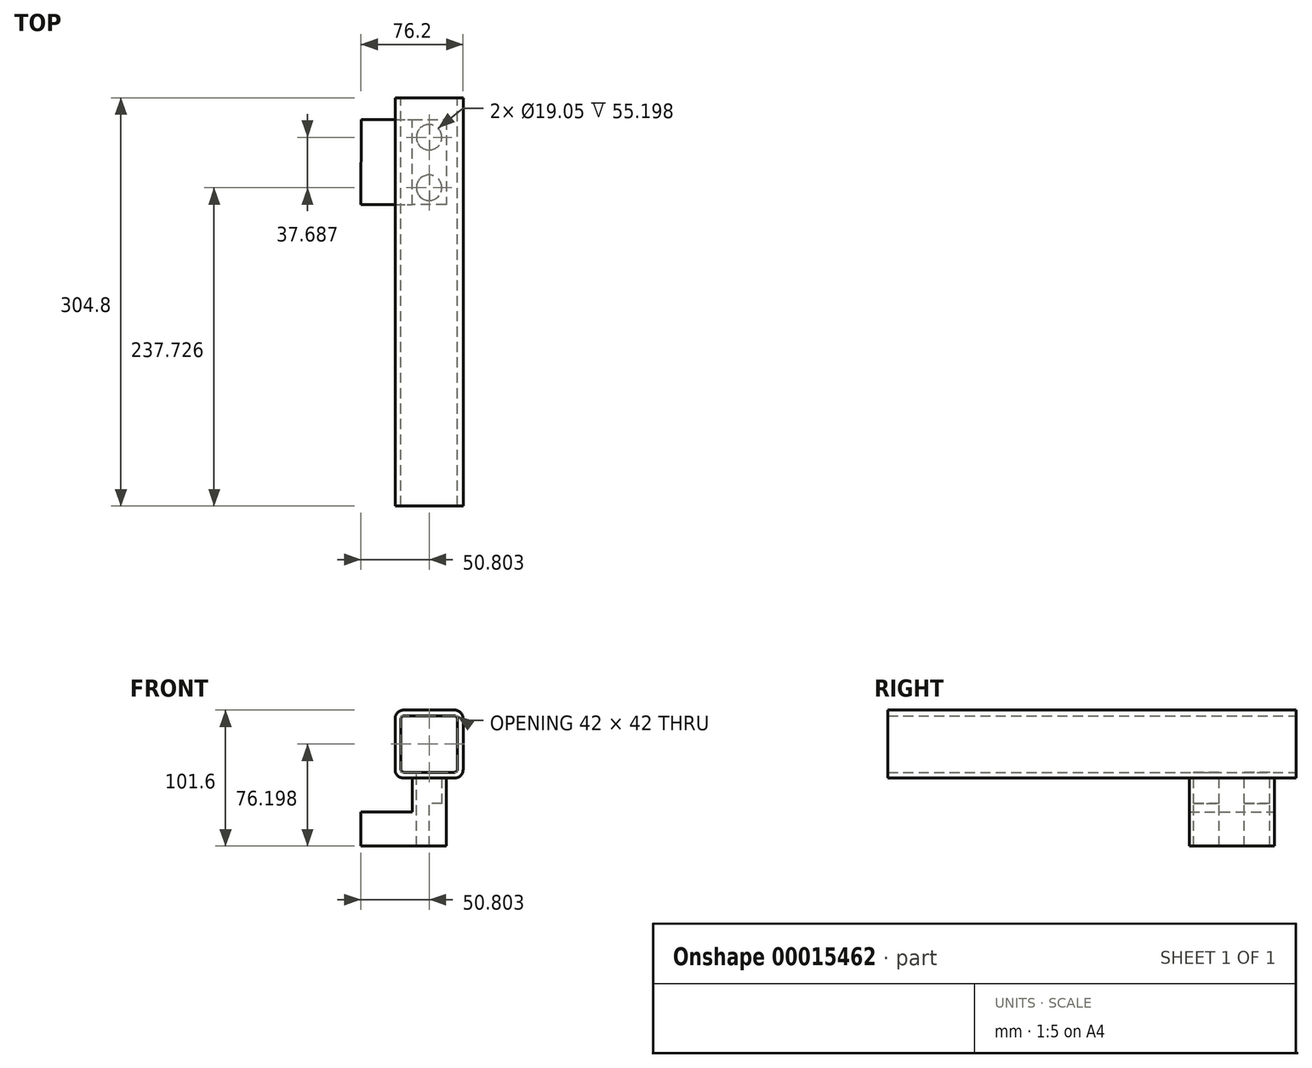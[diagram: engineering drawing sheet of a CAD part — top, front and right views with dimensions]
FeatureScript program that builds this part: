
annotation { "Feature Type Name" : "Feature", "Feature Type Description" : "" }
export const myFeature = defineFeature(function(context is Context, id is Id, definition is map)
    precondition{}
    {
        {
            var Q0;
            Q0=qCreatedBy(makeId("Front.planeOp"),FACE);
            var sketch = newSketch(context, id + "F0", { "sketchPlane" : qUnion([Q0])});
            skLineSegment(sketch, "E0", {"start": v(34.05, 28.16) * mm, "end": v(34.05, -9.94) * mm});
            skLineSegment(sketch, "E1", {"start": v(27.7, 34.5) * mm, "end": v(-10.4, 34.5) * mm});
            skLineSegment(sketch, "E2", {"start": v(-16.75, 28.16) * mm, "end": v(-16.75, -9.94) * mm});
            skLineSegment(sketch, "E3", {"start": v(-10.4, -16.3) * mm, "end": v(27.7, -16.3) * mm});
            skPoint(sketch, "E4.visualSharp", {"position": v(-16.75, 34.5) * mm});
            skArc(sketch, "E4.filletArc", {"start": v(-10.4, 34.5) * mm, "mid": v(-14.89, 32.65) * mm, "end": v(-16.75, 28.16) * mm});
            skPoint(sketch, "E5.visualSharp", {"position": v(34.05, 34.5) * mm});
            skArc(sketch, "E5.filletArc", {"start": v(34.05, 28.16) * mm, "mid": v(32.2, 32.65) * mm, "end": v(27.7, 34.5) * mm});
            skPoint(sketch, "E6.visualSharp", {"position": v(34.05, -16.3) * mm});
            skArc(sketch, "E6.filletArc", {"start": v(27.7, -16.3) * mm, "mid": v(32.2, -14.43) * mm, "end": v(34.05, -9.94) * mm});
            skPoint(sketch, "E7.visualSharp", {"position": v(-16.75, -16.3) * mm});
            skArc(sketch, "E7.filletArc", {"start": v(-16.75, -9.94) * mm, "mid": v(-14.89, -14.43) * mm, "end": v(-10.4, -16.3) * mm});
            skArc(sketch, "E8.0", {"start": v(29.66, 28.16) * mm, "mid": v(29.08, 29.54) * mm, "end": v(27.7, 30.1) * mm});
            skLineSegment(sketch, "E8.1", {"start": v(29.66, 28.16) * mm, "end": v(29.66, -9.94) * mm});
            skArc(sketch, "E8.2", {"start": v(27.7, -11.9) * mm, "mid": v(29.08, -11.32) * mm, "end": v(29.66, -9.94) * mm});
            skLineSegment(sketch, "E8.3", {"start": v(-10.4, -11.9) * mm, "end": v(27.7, -11.9) * mm});
            skArc(sketch, "E8.4", {"start": v(-12.35, -9.94) * mm, "mid": v(-11.78, -11.32) * mm, "end": v(-10.4, -11.9) * mm});
            skLineSegment(sketch, "E8.5", {"start": v(27.7, 30.1) * mm, "end": v(-10.4, 30.1) * mm});
            skLineSegment(sketch, "E8.6", {"start": v(-12.35, 28.16) * mm, "end": v(-12.35, -9.94) * mm});
            skArc(sketch, "E8.7", {"start": v(-10.4, 30.1) * mm, "mid": v(-11.78, 29.54) * mm, "end": v(-12.35, 28.16) * mm});
            skSolve(sketch);
        }
        {
            var Q0;
            Q0=makeQuery(id+"F0.imprint","IMPRINT",FACE,{"disambiguationData":[TD([[makeQuery(id+"F0.imprint","IMPRINT",EDGE,{"derivedFrom":sQuery(id+"F0.wireOp",EDGE,"E0")}),-1.0]])]});
            extrude(context, id + "F1", {"entities" : qUnion([Q0]), "depth" : 304.8 * mm});
        }
        {
            var Q0;
            Q0=makeQuery(id+"F1.opExtrude","SWEPT_FACE",FACE,{"disambiguationData":[OSD([sQuery(id+"F0.wireOp",EDGE,"E8.3")])]});
            var sketch = newSketch(context, id + "F2", { "sketchPlane" : qUnion([Q0])});
            skLineSegment(sketch, "E9", {"start": v(8.65, 0) * mm, "end": v(8.65, -127.32) * mm});
            skCircle(sketch, "E10", {"center": v(8.65, -29.39) * mm, "radius": 9.53 * mm});
            skCircle(sketch, "E11", {"center": v(8.65, -67.07) * mm, "radius": 9.53 * mm});
            skSolve(sketch);
        }
        {
            var Q0;
            Q0=sQuery(id+"F2.wireOp",VERTEX,"E11.center");
            var Q1;
            Q1=makeQuery(id+"F1.opExtrude","SWEPT_BODY",BODY,{"disambiguationData":[OSD([sQuery(id+"F0.wireOp",EDGE,"E0"),sQuery(id+"F0.wireOp",EDGE,"E1"),sQuery(id+"F0.wireOp",EDGE,"E2"),sQuery(id+"F0.wireOp",EDGE,"E3"),sQuery(id+"F0.wireOp",EDGE,"E4.filletArc"),sQuery(id+"F0.wireOp",EDGE,"E5.filletArc"),sQuery(id+"F0.wireOp",EDGE,"E6.filletArc"),sQuery(id+"F0.wireOp",EDGE,"E7.filletArc"),sQuery(id+"F0.wireOp",EDGE,"E8.0"),sQuery(id+"F0.wireOp",EDGE,"E8.1"),sQuery(id+"F0.wireOp",EDGE,"E8.2"),sQuery(id+"F0.wireOp",EDGE,"E8.3"),sQuery(id+"F0.wireOp",EDGE,"E8.4"),sQuery(id+"F0.wireOp",EDGE,"E8.5"),sQuery(id+"F0.wireOp",EDGE,"E8.6"),sQuery(id+"F0.wireOp",EDGE,"E8.7")])]});
            hole(context, id + "F3", {"style" : HoleStyle.SIMPLE, "holeDiameter" : 19.05 * mm, "endStyle" : HoleEndStyle.THROUGH, "locations" : qUnion([Q0]), "scope" : qUnion([Q1])});
        }
        {
            var Q0;
            Q0=sQuery(id+"F2.wireOp",VERTEX,"E10.center");
            var Q1;
            Q1=makeQuery(id+"F1.opExtrude","SWEPT_BODY",BODY,{"disambiguationData":[OSD([sQuery(id+"F0.wireOp",EDGE,"E0"),sQuery(id+"F0.wireOp",EDGE,"E1"),sQuery(id+"F0.wireOp",EDGE,"E2"),sQuery(id+"F0.wireOp",EDGE,"E3"),sQuery(id+"F0.wireOp",EDGE,"E4.filletArc"),sQuery(id+"F0.wireOp",EDGE,"E5.filletArc"),sQuery(id+"F0.wireOp",EDGE,"E6.filletArc"),sQuery(id+"F0.wireOp",EDGE,"E7.filletArc"),sQuery(id+"F0.wireOp",EDGE,"E8.0"),sQuery(id+"F0.wireOp",EDGE,"E8.1"),sQuery(id+"F0.wireOp",EDGE,"E8.2"),sQuery(id+"F0.wireOp",EDGE,"E8.3"),sQuery(id+"F0.wireOp",EDGE,"E8.4"),sQuery(id+"F0.wireOp",EDGE,"E8.5"),sQuery(id+"F0.wireOp",EDGE,"E8.6"),sQuery(id+"F0.wireOp",EDGE,"E8.7")])]});
            hole(context, id + "F4", {"style" : HoleStyle.SIMPLE, "holeDiameter" : 19.05 * mm, "endStyle" : HoleEndStyle.THROUGH, "locations" : qUnion([Q0]), "scope" : qUnion([Q1])});
        }
        {
            var Q0;
            Q0=makeQuery(id+"F1.opExtrude","SWEPT_FACE",FACE,{"disambiguationData":[OSD([sQuery(id+"F0.wireOp",EDGE,"E3")])]});
            var sketch = newSketch(context, id + "F5", { "sketchPlane" : qUnion([Q0])});
            skLineSegment(sketch, "E12", {"start": v(21.35, 29.39) * mm, "end": v(21.35, 16.33) * mm, "construction": true});
            skLineSegment(sketch, "E13", {"start": v(21.35, 16.33) * mm, "end": v(-3.9, 16.33) * mm, "construction": true});
            skLineSegment(sketch, "E14", {"start": v(-3.9, 16.33) * mm, "end": v(-4.05, 27.58) * mm, "construction": true});
            skPoint(sketch, "E15.start.orphan", {"position": v(8.65, 29.39) * mm});
            skLineSegment(sketch, "E16", {"start": v(-4.05, 27.58) * mm, "end": v(-4.05, 79.83) * mm, "construction": true});
            skLineSegment(sketch, "E17", {"start": v(-4.05, 79.83) * mm, "end": v(8.65, 79.83) * mm, "construction": true});
            skLineSegment(sketch, "E18", {"start": v(21.35, 29.39) * mm, "end": v(21.35, 79.83) * mm, "construction": true});
            skLineSegment(sketch, "E19", {"start": v(8.65, 79.83) * mm, "end": v(21.35, 79.83) * mm, "construction": true});
            skPoint(sketch, "E20.orphan", {"position": v(8.65, 16.33) * mm});
            skPoint(sketch, "E21.end.orphan", {"position": v(8.65, 67.07) * mm});
            skLineSegment(sketch, "E22", {"start": v(-3.9, 16.33) * mm, "end": v(21.35, 16.33) * mm});
            skLineSegment(sketch, "E23", {"start": v(21.35, 16.33) * mm, "end": v(21.35, 79.83) * mm});
            skLineSegment(sketch, "E24", {"start": v(21.35, 79.83) * mm, "end": v(-4.05, 79.83) * mm});
            skLineSegment(sketch, "E25", {"start": v(-4.05, 79.83) * mm, "end": v(-3.9, 16.33) * mm});
            skSolve(sketch);
        }
        {
            var Q0;
            Q0=makeQuery(id+"F5.imprint","IMPRINT",FACE,{"disambiguationData":[TD([[makeQuery(id+"F5.imprint","IMPRINT",EDGE,{"derivedFrom":sQuery(id+"F5.wireOp",EDGE,"E22")}),1.0]])]});
            extrude(context, id + "F6", {"entities" : qUnion([Q0]), "operationType" : NewBodyOperationType.ADD, "depth" : 19.05 * mm});
        }
        {
            var Q0;
            Q0=makeQuery(id+"F6.opExtrude","CAP_FACE",FACE,{"disambiguationData":[OSD([sQuery(id+"F0.wireOp",EDGE,"E3"),sQuery(id+"F3.hole-0.sketch.wireOp",EDGE,"core_line_2"),sQuery(id+"F4.hole-0.sketch.wireOp",EDGE,"core_line_2"),sQuery(id+"F5.wireOp",EDGE,"E22"),sQuery(id+"F5.wireOp",EDGE,"E23"),sQuery(id+"F5.wireOp",EDGE,"E24"),sQuery(id+"F5.wireOp",EDGE,"E25")])],"isStart":false});
            var sketch = newSketch(context, id + "F7", { "sketchPlane" : qUnion([Q0])});
            skArc(sketch, "E26.0.0", {"start": v(8.65, 76.6) * mm, "mid": v(18.18, 67.07) * mm, "end": v(8.65, 57.55) * mm});
            skLineSegment(sketch, "E26.0.1", {"start": v(8.65, 57.55) * mm, "end": v(8.65, 76.6) * mm});
            skLineSegment(sketch, "E27.0.0", {"start": v(8.65, 76.6) * mm, "end": v(8.65, 57.55) * mm});
            skArc(sketch, "E27.0.1", {"start": v(8.65, 57.55) * mm, "mid": v(-0.87, 67.07) * mm, "end": v(8.65, 76.6) * mm});
            skArc(sketch, "E28.0.0", {"start": v(8.65, 38.91) * mm, "mid": v(18.18, 29.39) * mm, "end": v(8.65, 19.86) * mm});
            skLineSegment(sketch, "E28.0.1", {"start": v(8.65, 19.86) * mm, "end": v(8.65, 38.91) * mm});
            skLineSegment(sketch, "E29.0.0", {"start": v(8.65, 38.91) * mm, "end": v(8.65, 19.86) * mm});
            skArc(sketch, "E29.0.1", {"start": v(8.65, 19.86) * mm, "mid": v(-0.87, 29.39) * mm, "end": v(8.65, 38.91) * mm});
            skSolve(sketch);
        }
        {
            var Q0;
            Q0=makeQuery(id+"F7.imprint","IMPRINT",FACE,{"disambiguationData":[TD([[makeQuery(id+"F7.imprint","IMPRINT",EDGE,{"derivedFrom":sQuery(id+"F7.wireOp",EDGE,"E26.0.0")}),1.0]])]});
            var Q1;
            Q1=makeQuery(id+"F7.imprint","IMPRINT",FACE,{"disambiguationData":[TD([[makeQuery(id+"F7.imprint","IMPRINT",EDGE,{"derivedFrom":sQuery(id+"F7.wireOp",EDGE,"E27.0.0")}),-1.0]])]});
            var Q2;
            Q2=makeQuery(id+"F7.imprint","IMPRINT",FACE,{"disambiguationData":[TD([[makeQuery(id+"F7.imprint","IMPRINT",EDGE,{"derivedFrom":sQuery(id+"F7.wireOp",EDGE,"E28.0.0")}),1.0]])]});
            var Q3;
            Q3=makeQuery(id+"F7.imprint","IMPRINT",FACE,{"disambiguationData":[TD([[makeQuery(id+"F7.imprint","IMPRINT",EDGE,{"derivedFrom":sQuery(id+"F7.wireOp",EDGE,"E29.0.0")}),-1.0]])]});
            var Q4;
            Q4=makeQuery(id+"F7.imprint","IMPRINT",FACE,{"disambiguationData":[TD([[makeQuery(id+"F7.imprint","IMPRINT",EDGE,{"derivedFrom":sQuery(id+"F7.wireOp",EDGE,"E26.0.0")}),-1.0]])]});
            extrude(context, id + "F8", {"entities" : qUnion([Q0, Q1, Q2, Q3, Q4]), "operationType" : NewBodyOperationType.ADD, "depth" : 6.35 * mm});
        }
        {
            var Q0;
            Q0=makeQuery(id+"F8.opExtrude","CAP_FACE",FACE,{"disambiguationData":[OSD([sQuery(id+"F5.wireOp",EDGE,"E22"),sQuery(id+"F5.wireOp",EDGE,"E23"),sQuery(id+"F5.wireOp",EDGE,"E24"),sQuery(id+"F5.wireOp",EDGE,"E25")])],"isStart":false});
            extrude(context, id + "F9", {"entities" : qUnion([Q0]), "operationType" : NewBodyOperationType.ADD, "depth" : 25.4 * mm});
        }
        {
            var Q0;
            {var subQ0=sQuery(id+"F5.wireOp",EDGE,"E25");Q0=makeQuery(id+"F9.boolean.opBoolean","MERGE",FACE,{"derivedFrom":[makeQuery(id+"F8.boolean.opBoolean","MERGE",FACE,{"derivedFrom":[makeQuery(id+"F6.opExtrude","SWEPT_FACE",FACE,{"disambiguationData":[OSD([subQ0])]}),makeQuery(id+"F8.opExtrude","SWEPT_FACE",FACE,{"disambiguationData":[OSD([subQ0])]})]}),makeQuery(id+"F9.opExtrude","SWEPT_FACE",FACE,{"disambiguationData":[OSD([subQ0])]})]});}
            var sketch = newSketch(context, id + "F10", { "sketchPlane" : qUnion([Q0])});
            skLineSegment(sketch, "E30", {"start": v(79.84, -41.7) * mm, "end": v(16.34, -41.7) * mm});
            skSolve(sketch);
        }
        {
            var Q0;
            {var subQ3=sQuery(id+"F10.wireOp",EDGE,"E30");Q0=makeQuery(id+"F10.imprint","IMPRINT",FACE,{"disambiguationData":[TD([[makeQuery(id+"F10.imprint","IMPRINT",EDGE,{"derivedFrom":subQ3}),1.0]])]});}
            extrude(context, id + "F11", {"entities" : qUnion([Q0]), "operationType" : NewBodyOperationType.ADD, "depth" : 38.1 * mm});
        }
    });
